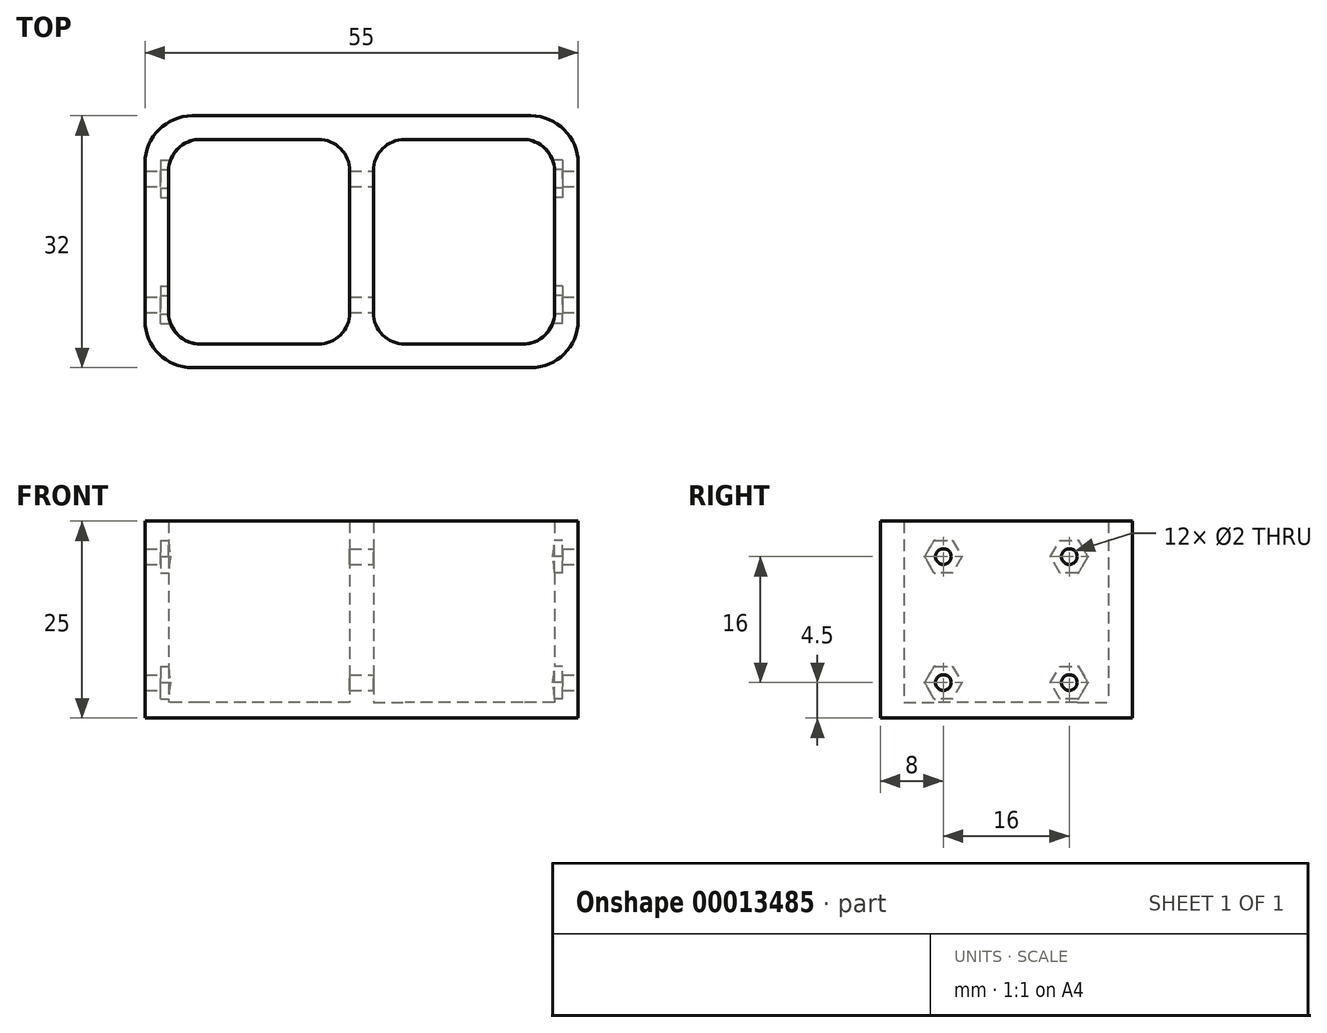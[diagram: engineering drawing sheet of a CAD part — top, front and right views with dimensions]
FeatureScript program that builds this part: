
annotation { "Feature Type Name" : "Feature", "Feature Type Description" : "" }
export const myFeature = defineFeature(function(context is Context, id is Id, definition is map)
    precondition{}
    {
        {
            var Q0;
            Q0=qCreatedBy(makeId("Top.planeOp"),FACE);
            var sketch = newSketch(context, id + "F0", { "sketchPlane" : qUnion([Q0])});
            skLineSegment(sketch, "E0.rect.bottom", {"start": v(20.5, 13) * mm, "end": v(5.5, 13) * mm});
            skLineSegment(sketch, "E0.rect.top", {"start": v(20.5, -13) * mm, "end": v(5.5, -13) * mm});
            skLineSegment(sketch, "E0.rect.left", {"start": v(24.5, 9) * mm, "end": v(24.5, -9) * mm});
            skLineSegment(sketch, "E0.rect.right", {"start": v(-24.5, 9) * mm, "end": v(-24.5, -9) * mm});
            skPoint(sketch, "E0.rect.middle", {"position": v(0, 0) * mm});
            skLineSegment(sketch, "E1.rect.bottom", {"start": v(21.5, 16) * mm, "end": v(-21.5, 16) * mm});
            skLineSegment(sketch, "E1.rect.top", {"start": v(21.5, -16) * mm, "end": v(-21.5, -16) * mm});
            skLineSegment(sketch, "E1.rect.left", {"start": v(27.5, 10) * mm, "end": v(27.5, -10) * mm});
            skLineSegment(sketch, "E1.rect.right", {"start": v(-27.5, 10) * mm, "end": v(-27.5, -10) * mm});
            skPoint(sketch, "E2.visualSharp", {"position": v(-24.5, 13) * mm});
            skArc(sketch, "E2.filletArc", {"start": v(-20.5, 13) * mm, "mid": v(-23.33, 11.83) * mm, "end": v(-24.5, 9) * mm});
            skPoint(sketch, "E3.visualSharp", {"position": v(24.5, 13) * mm});
            skArc(sketch, "E3.filletArc", {"start": v(24.5, 9) * mm, "mid": v(23.33, 11.83) * mm, "end": v(20.5, 13) * mm});
            skPoint(sketch, "E4.visualSharp", {"position": v(24.5, -13) * mm});
            skArc(sketch, "E4.filletArc", {"start": v(20.5, -13) * mm, "mid": v(23.33, -11.83) * mm, "end": v(24.5, -9) * mm});
            skPoint(sketch, "E5.visualSharp", {"position": v(-24.5, -13) * mm});
            skArc(sketch, "E5.filletArc", {"start": v(-24.5, -9) * mm, "mid": v(-23.33, -11.83) * mm, "end": v(-20.5, -13) * mm});
            skPoint(sketch, "E6.visualSharp", {"position": v(-27.5, 16) * mm});
            skArc(sketch, "E6.filletArc", {"start": v(-21.5, 16) * mm, "mid": v(-25.74, 14.24) * mm, "end": v(-27.5, 10) * mm});
            skPoint(sketch, "E7.visualSharp", {"position": v(27.5, 16) * mm});
            skArc(sketch, "E7.filletArc", {"start": v(27.5, 10) * mm, "mid": v(25.74, 14.24) * mm, "end": v(21.5, 16) * mm});
            skPoint(sketch, "E8.visualSharp", {"position": v(27.5, -16) * mm});
            skArc(sketch, "E8.filletArc", {"start": v(21.5, -16) * mm, "mid": v(25.74, -14.24) * mm, "end": v(27.5, -10) * mm});
            skPoint(sketch, "E9.visualSharp", {"position": v(-27.5, -16) * mm});
            skArc(sketch, "E9.filletArc", {"start": v(-27.5, -10) * mm, "mid": v(-25.74, -14.24) * mm, "end": v(-21.5, -16) * mm});
            skLineSegment(sketch, "E10", {"start": v(-1.5, 9) * mm, "end": v(-1.5, -9) * mm});
            skLineSegment(sketch, "E11", {"start": v(1.5, 9) * mm, "end": v(1.5, -9) * mm});
            skLineSegment(sketch, "E12.trimOffspring", {"start": v(-5.5, 13) * mm, "end": v(-20.5, 13) * mm});
            skLineSegment(sketch, "E13.trimOffspring", {"start": v(-5.5, -13) * mm, "end": v(-20.5, -13) * mm});
            skPoint(sketch, "E14.visualSharp", {"position": v(-1.5, 13) * mm});
            skArc(sketch, "E14.filletArc", {"start": v(-1.5, 9) * mm, "mid": v(-2.67, 11.83) * mm, "end": v(-5.5, 13) * mm});
            skPoint(sketch, "E15.visualSharp", {"position": v(1.5, 13) * mm});
            skArc(sketch, "E15.filletArc", {"start": v(5.5, 13) * mm, "mid": v(2.67, 11.83) * mm, "end": v(1.5, 9) * mm});
            skPoint(sketch, "E16.visualSharp", {"position": v(1.5, -13) * mm});
            skArc(sketch, "E16.filletArc", {"start": v(1.5, -9) * mm, "mid": v(2.67, -11.83) * mm, "end": v(5.5, -13) * mm});
            skPoint(sketch, "E17.visualSharp", {"position": v(-1.5, -13) * mm});
            skArc(sketch, "E17.filletArc", {"start": v(-5.5, -13) * mm, "mid": v(-2.67, -11.83) * mm, "end": v(-1.5, -9) * mm});
            skSolve(sketch);
        }
        {
            var Q0;
            Q0=makeQuery(id+"F0.imprint","IMPRINT",FACE,{"disambiguationData":[TD([[makeQuery(id+"F0.imprint","IMPRINT",EDGE,{"derivedFrom":sQuery(id+"F0.wireOp",EDGE,"E0.rect.bottom")}),-1.0]])]});
            extrude(context, id + "F1", {"entities" : qUnion([Q0]), "depth" : 25 * mm});
        }
        {
            var Q0;
            Q0=makeQuery(id+"F0.imprint","IMPRINT",FACE,{"disambiguationData":[TD([[makeQuery(id+"F0.imprint","IMPRINT",EDGE,{"derivedFrom":sQuery(id+"F0.wireOp",EDGE,"E0.rect.bottom")}),1.0]])]});
            var Q1;
            Q1=makeQuery(id+"F0.imprint","IMPRINT",FACE,{"disambiguationData":[TD([[makeQuery(id+"F0.imprint","IMPRINT",EDGE,{"derivedFrom":sQuery(id+"F0.wireOp",EDGE,"E0.rect.right")}),1.0]])]});
            extrude(context, id + "F2", {"entities" : qUnion([Q0, Q1]), "operationType" : NewBodyOperationType.ADD, "depth" : 2 * mm});
        }
        {
            var Q0;
            Q0=makeQuery(id+"F1.opExtrude","SWEPT_FACE",FACE,{"disambiguationData":[OSD([sQuery(id+"F0.wireOp",EDGE,"E1.rect.left")])]});
            var sketch = newSketch(context, id + "F3", { "sketchPlane" : qUnion([Q0])});
            skLineSegment(sketch, "E18.rect.bottom", {"start": v(8, 4.5) * mm, "end": v(-8, 4.5) * mm, "construction": true});
            skLineSegment(sketch, "E18.rect.top", {"start": v(8, 20.5) * mm, "end": v(-8, 20.5) * mm, "construction": true});
            skLineSegment(sketch, "E18.rect.left", {"start": v(8, 4.5) * mm, "end": v(8, 20.5) * mm, "construction": true});
            skLineSegment(sketch, "E18.rect.right", {"start": v(-8, 4.5) * mm, "end": v(-8, 20.5) * mm, "construction": true});
            skPoint(sketch, "E18.rect.middle", {"position": v(0, 12.5) * mm});
            skLineSegment(sketch, "E19", {"start": v(0, 0) * mm, "end": v(0, 25) * mm, "construction": true});
            skCircle(sketch, "E20", {"center": v(8, 20.5) * mm, "radius": 1 * mm});
            skCircle(sketch, "E21", {"center": v(8, 4.5) * mm, "radius": 1 * mm});
            skCircle(sketch, "E22", {"center": v(-8, 4.5) * mm, "radius": 1 * mm});
            skCircle(sketch, "E23", {"center": v(-8, 20.5) * mm, "radius": 1 * mm});
            skSolve(sketch);
        }
        {
            var Q0;
            Q0 = qSketchRegion(id + "F3", true);
            extrude(context, id + "F4", {"entities" : qUnion([Q0]), "operationType" : NewBodyOperationType.REMOVE, "endBound" : BoundingType.THROUGH_ALL, "oppositeDirection" : true, "depth" : 25 * mm});
        }
        {
            var Q0;
            Q0=makeQuery(id+"F1.opExtrude","SWEPT_FACE",FACE,{"disambiguationData":[OSD([sQuery(id+"F0.wireOp",EDGE,"E0.rect.right")])]});
            var sketch = newSketch(context, id + "F5", { "sketchPlane" : qUnion([Q0])});
            skCircle(sketch, "E24.cCircle", {"center": v(-8, 20.5) * mm, "radius": 2.05 * mm, "construction": true});
            skLineSegment(sketch, "E24.0", {"start": v(-6.82, 22.55) * mm, "end": v(-5.63, 20.5) * mm});
            skLineSegment(sketch, "E24.1", {"start": v(-5.63, 20.5) * mm, "end": v(-6.82, 18.45) * mm});
            skLineSegment(sketch, "E24.2", {"start": v(-6.82, 18.45) * mm, "end": v(-9.18, 18.45) * mm});
            skLineSegment(sketch, "E24.3", {"start": v(-9.18, 18.45) * mm, "end": v(-10.37, 20.5) * mm});
            skLineSegment(sketch, "E24.4", {"start": v(-10.37, 20.5) * mm, "end": v(-9.18, 22.55) * mm});
            skLineSegment(sketch, "E24.5", {"start": v(-9.18, 22.55) * mm, "end": v(-6.82, 22.55) * mm});
            skPoint(sketch, "E24.0.midPoint", {"position": v(-6.22, 21.52) * mm});
            skCircle(sketch, "E25.cCircle", {"center": v(8, 20.5) * mm, "radius": 2.05 * mm, "construction": true});
            skLineSegment(sketch, "E25.0", {"start": v(6.82, 22.55) * mm, "end": v(9.18, 22.55) * mm});
            skLineSegment(sketch, "E25.1", {"start": v(9.18, 22.55) * mm, "end": v(10.37, 20.5) * mm});
            skLineSegment(sketch, "E25.2", {"start": v(10.37, 20.5) * mm, "end": v(9.18, 18.45) * mm});
            skLineSegment(sketch, "E25.3", {"start": v(9.18, 18.45) * mm, "end": v(6.82, 18.45) * mm});
            skLineSegment(sketch, "E25.4", {"start": v(6.82, 18.45) * mm, "end": v(5.63, 20.5) * mm});
            skLineSegment(sketch, "E25.5", {"start": v(5.63, 20.5) * mm, "end": v(6.82, 22.55) * mm});
            skPoint(sketch, "E25.0.midPoint", {"position": v(8, 22.55) * mm});
            skCircle(sketch, "E26.cCircle", {"center": v(-8, 4.5) * mm, "radius": 2.05 * mm, "construction": true});
            skLineSegment(sketch, "E26.0", {"start": v(-9.18, 6.55) * mm, "end": v(-6.82, 6.55) * mm});
            skLineSegment(sketch, "E26.1", {"start": v(-6.82, 6.55) * mm, "end": v(-5.63, 4.5) * mm});
            skLineSegment(sketch, "E26.2", {"start": v(-5.63, 4.5) * mm, "end": v(-6.82, 2.45) * mm});
            skLineSegment(sketch, "E26.3", {"start": v(-6.82, 2.45) * mm, "end": v(-9.18, 2.45) * mm});
            skLineSegment(sketch, "E26.4", {"start": v(-9.18, 2.45) * mm, "end": v(-10.37, 4.5) * mm});
            skLineSegment(sketch, "E26.5", {"start": v(-10.37, 4.5) * mm, "end": v(-9.18, 6.55) * mm});
            skPoint(sketch, "E26.0.midPoint", {"position": v(-8, 6.55) * mm});
            skCircle(sketch, "E27.cCircle", {"center": v(8, 4.5) * mm, "radius": 2.05 * mm, "construction": true});
            skLineSegment(sketch, "E27.0", {"start": v(6.82, 6.55) * mm, "end": v(9.18, 6.55) * mm});
            skLineSegment(sketch, "E27.1", {"start": v(9.18, 6.55) * mm, "end": v(10.37, 4.5) * mm});
            skLineSegment(sketch, "E27.2", {"start": v(10.37, 4.5) * mm, "end": v(9.18, 2.45) * mm});
            skLineSegment(sketch, "E27.3", {"start": v(9.18, 2.45) * mm, "end": v(6.82, 2.45) * mm});
            skLineSegment(sketch, "E27.4", {"start": v(6.82, 2.45) * mm, "end": v(5.63, 4.5) * mm});
            skLineSegment(sketch, "E27.5", {"start": v(5.63, 4.5) * mm, "end": v(6.82, 6.55) * mm});
            skPoint(sketch, "E27.0.midPoint", {"position": v(8, 6.55) * mm});
            skSolve(sketch);
        }
        {
            var Q0;
            Q0 = qSketchRegion(id + "F5", true);
            extrude(context, id + "F6", {"entities" : qUnion([Q0]), "operationType" : NewBodyOperationType.REMOVE, "endBound" : BoundingType.SYMMETRIC, "oppositeDirection" : true, "depth" : 2 * mm});
        }
        {
            var Q0;
            Q0=makeQuery(id+"F1.opExtrude","SWEPT_FACE",FACE,{"disambiguationData":[OSD([sQuery(id+"F0.wireOp",EDGE,"E0.rect.left")])]});
            var sketch = newSketch(context, id + "F7", { "sketchPlane" : qUnion([Q0])});
            skCircle(sketch, "E28.cCircle", {"center": v(-8, 20.5) * mm, "radius": 2.05 * mm, "construction": true});
            skLineSegment(sketch, "E28.0", {"start": v(-9.18, 22.55) * mm, "end": v(-6.82, 22.55) * mm});
            skLineSegment(sketch, "E28.1", {"start": v(-6.82, 22.55) * mm, "end": v(-5.63, 20.5) * mm});
            skLineSegment(sketch, "E28.2", {"start": v(-5.63, 20.5) * mm, "end": v(-6.82, 18.45) * mm});
            skLineSegment(sketch, "E28.3", {"start": v(-6.82, 18.45) * mm, "end": v(-9.18, 18.45) * mm});
            skLineSegment(sketch, "E28.4", {"start": v(-9.18, 18.45) * mm, "end": v(-10.37, 20.5) * mm});
            skLineSegment(sketch, "E28.5", {"start": v(-10.37, 20.5) * mm, "end": v(-9.18, 22.55) * mm});
            skPoint(sketch, "E28.0.midPoint", {"position": v(-8, 22.55) * mm});
            skCircle(sketch, "E29.cCircle", {"center": v(8, 20.5) * mm, "radius": 2.05 * mm, "construction": true});
            skLineSegment(sketch, "E29.0", {"start": v(6.82, 22.55) * mm, "end": v(9.18, 22.55) * mm});
            skLineSegment(sketch, "E29.1", {"start": v(9.18, 22.55) * mm, "end": v(10.37, 20.5) * mm});
            skLineSegment(sketch, "E29.2", {"start": v(10.37, 20.5) * mm, "end": v(9.18, 18.45) * mm});
            skLineSegment(sketch, "E29.3", {"start": v(9.18, 18.45) * mm, "end": v(6.82, 18.45) * mm});
            skLineSegment(sketch, "E29.4", {"start": v(6.82, 18.45) * mm, "end": v(5.63, 20.5) * mm});
            skLineSegment(sketch, "E29.5", {"start": v(5.63, 20.5) * mm, "end": v(6.82, 22.55) * mm});
            skPoint(sketch, "E29.0.midPoint", {"position": v(8, 22.55) * mm});
            skCircle(sketch, "E30.cCircle", {"center": v(-8, 4.5) * mm, "radius": 2.05 * mm, "construction": true});
            skLineSegment(sketch, "E30.0", {"start": v(-9.18, 6.55) * mm, "end": v(-6.82, 6.55) * mm});
            skLineSegment(sketch, "E30.1", {"start": v(-6.82, 6.55) * mm, "end": v(-5.63, 4.5) * mm});
            skLineSegment(sketch, "E30.2", {"start": v(-5.63, 4.5) * mm, "end": v(-6.82, 2.45) * mm});
            skLineSegment(sketch, "E30.3", {"start": v(-6.82, 2.45) * mm, "end": v(-9.18, 2.45) * mm});
            skLineSegment(sketch, "E30.4", {"start": v(-9.18, 2.45) * mm, "end": v(-10.37, 4.5) * mm});
            skLineSegment(sketch, "E30.5", {"start": v(-10.37, 4.5) * mm, "end": v(-9.18, 6.55) * mm});
            skPoint(sketch, "E30.0.midPoint", {"position": v(-8, 6.55) * mm});
            skCircle(sketch, "E31.cCircle", {"center": v(8, 4.5) * mm, "radius": 2.05 * mm, "construction": true});
            skLineSegment(sketch, "E31.0", {"start": v(6.82, 6.55) * mm, "end": v(9.18, 6.55) * mm});
            skLineSegment(sketch, "E31.1", {"start": v(9.18, 6.55) * mm, "end": v(10.37, 4.5) * mm});
            skLineSegment(sketch, "E31.2", {"start": v(10.37, 4.5) * mm, "end": v(9.18, 2.45) * mm});
            skLineSegment(sketch, "E31.3", {"start": v(9.18, 2.45) * mm, "end": v(6.82, 2.45) * mm});
            skLineSegment(sketch, "E31.4", {"start": v(6.82, 2.45) * mm, "end": v(5.63, 4.5) * mm});
            skLineSegment(sketch, "E31.5", {"start": v(5.63, 4.5) * mm, "end": v(6.82, 6.55) * mm});
            skPoint(sketch, "E31.0.midPoint", {"position": v(8, 6.55) * mm});
            skSolve(sketch);
        }
        {
            var Q0;
            Q0 = qSketchRegion(id + "F7", true);
            extrude(context, id + "F8", {"entities" : qUnion([Q0]), "operationType" : NewBodyOperationType.REMOVE, "endBound" : BoundingType.SYMMETRIC, "oppositeDirection" : true, "depth" : 2 * mm});
        }
    });
